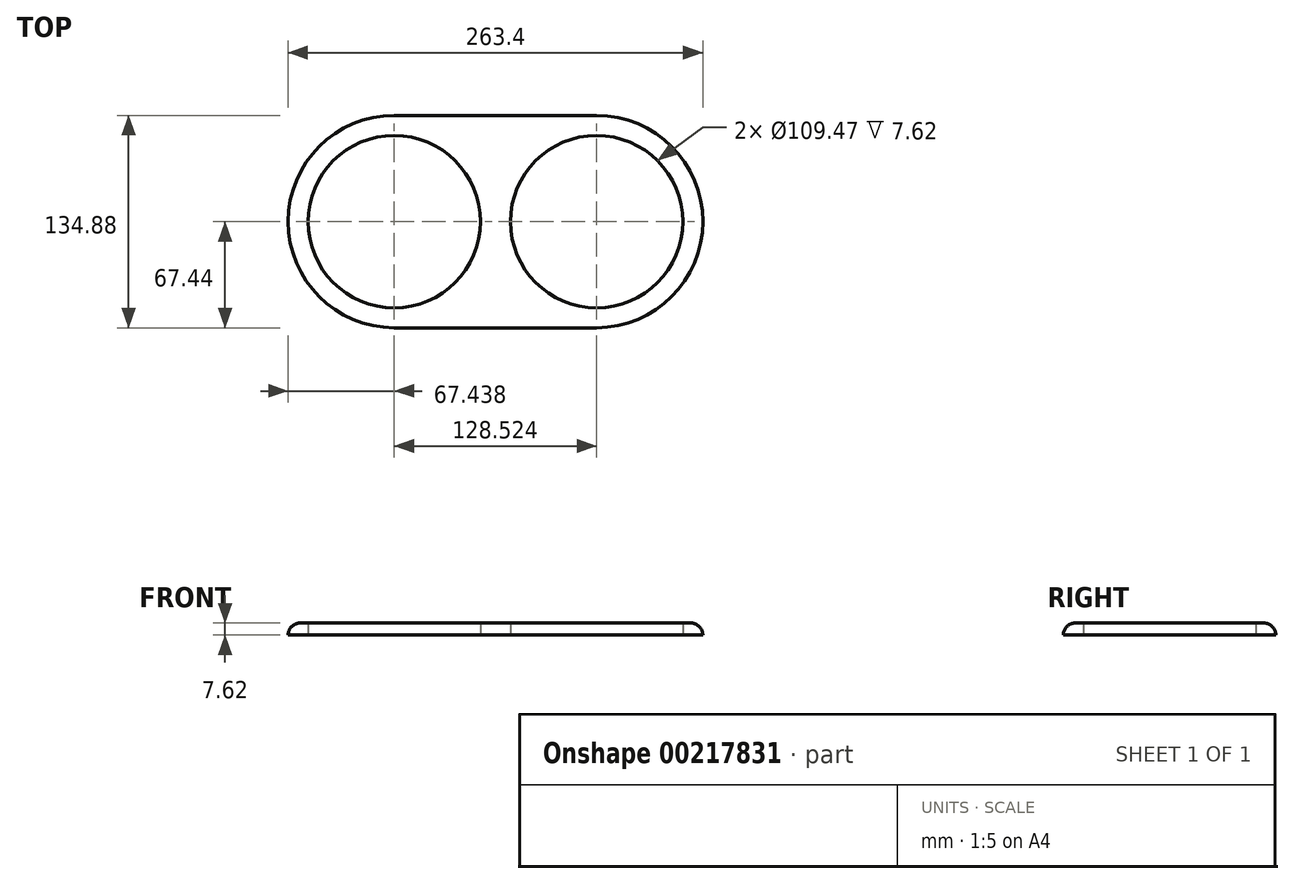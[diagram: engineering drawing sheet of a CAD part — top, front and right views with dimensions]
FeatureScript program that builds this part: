
annotation { "Feature Type Name" : "Feature", "Feature Type Description" : "" }
export const myFeature = defineFeature(function(context is Context, id is Id, definition is map)
    precondition{}
    {
        {
            var Q0;
            Q0=qCreatedBy(makeId("Top.planeOp"),FACE);
            var sketch = newSketch(context, id + "F0", { "sketchPlane" : qUnion([Q0])});
            skPoint(sketch, "E0", {"position": v(-9.53, 0) * mm});
            skLineSegment(sketch, "E1", {"start": v(64.26, 54.74) * mm, "end": v(-64.26, 54.74) * mm});
            skLineSegment(sketch, "E2", {"start": v(64.26, -54.74) * mm, "end": v(-64.26, -54.74) * mm});
            skArc(sketch, "E3", {"start": v(64.26, -54.74) * mm, "mid": v(119, 0) * mm, "end": v(64.26, 54.74) * mm});
            skArc(sketch, "E4", {"start": v(64.26, 54.74) * mm, "mid": v(9.53, 0) * mm, "end": v(64.26, -54.74) * mm});
            skArc(sketch, "E5", {"start": v(-64.26, -54.74) * mm, "mid": v(-9.53, 0) * mm, "end": v(-64.26, 54.74) * mm});
            skArc(sketch, "E6", {"start": v(-64.26, 54.74) * mm, "mid": v(-119, 0) * mm, "end": v(-64.26, -54.74) * mm});
            skLineSegment(sketch, "E7.0", {"start": v(64.26, 67.44) * mm, "end": v(-64.26, 67.44) * mm});
            skArc(sketch, "E7.1", {"start": v(64.26, -67.44) * mm, "mid": v(131.7, 0) * mm, "end": v(64.26, 67.44) * mm});
            skLineSegment(sketch, "E7.2", {"start": v(64.26, -67.44) * mm, "end": v(-64.26, -67.44) * mm});
            skArc(sketch, "E7.3", {"start": v(-64.26, 67.44) * mm, "mid": v(-131.7, 0) * mm, "end": v(-64.26, -67.44) * mm});
            skSolve(sketch);
        }
        {
            var Q0;
            Q0=makeQuery(id+"F0.imprint","IMPRINT",FACE,{"disambiguationData":[TD([[makeQuery(id+"F0.imprint","IMPRINT",EDGE,{"derivedFrom":sQuery(id+"F0.wireOp",EDGE,"E1")}),-1.0]])]});
            var Q1;
            Q1=makeQuery(id+"F0.imprint","IMPRINT",FACE,{"disambiguationData":[TD([[makeQuery(id+"F0.imprint","IMPRINT",EDGE,{"derivedFrom":sQuery(id+"F0.wireOp",EDGE,"E1")}),1.0]])]});
            extrude(context, id + "F1", {"entities" : qUnion([Q0, Q1]), "depth" : 7.62 * mm});
        }
        {
            var Q0;
            Q0=makeQuery(id+"F1.opExtrude","CAP_EDGE",EDGE,{"disambiguationData":[OSD([sQuery(id+"F0.wireOp",EDGE,"E7.3")])],"isStart":false});
            fillet(context, id + "F2", {"entities" : qUnion([Q0]), "radius" : 7.62 * mm, "tangentPropagation" : true, "allowEdgeOverflow" : false});
        }
    });
